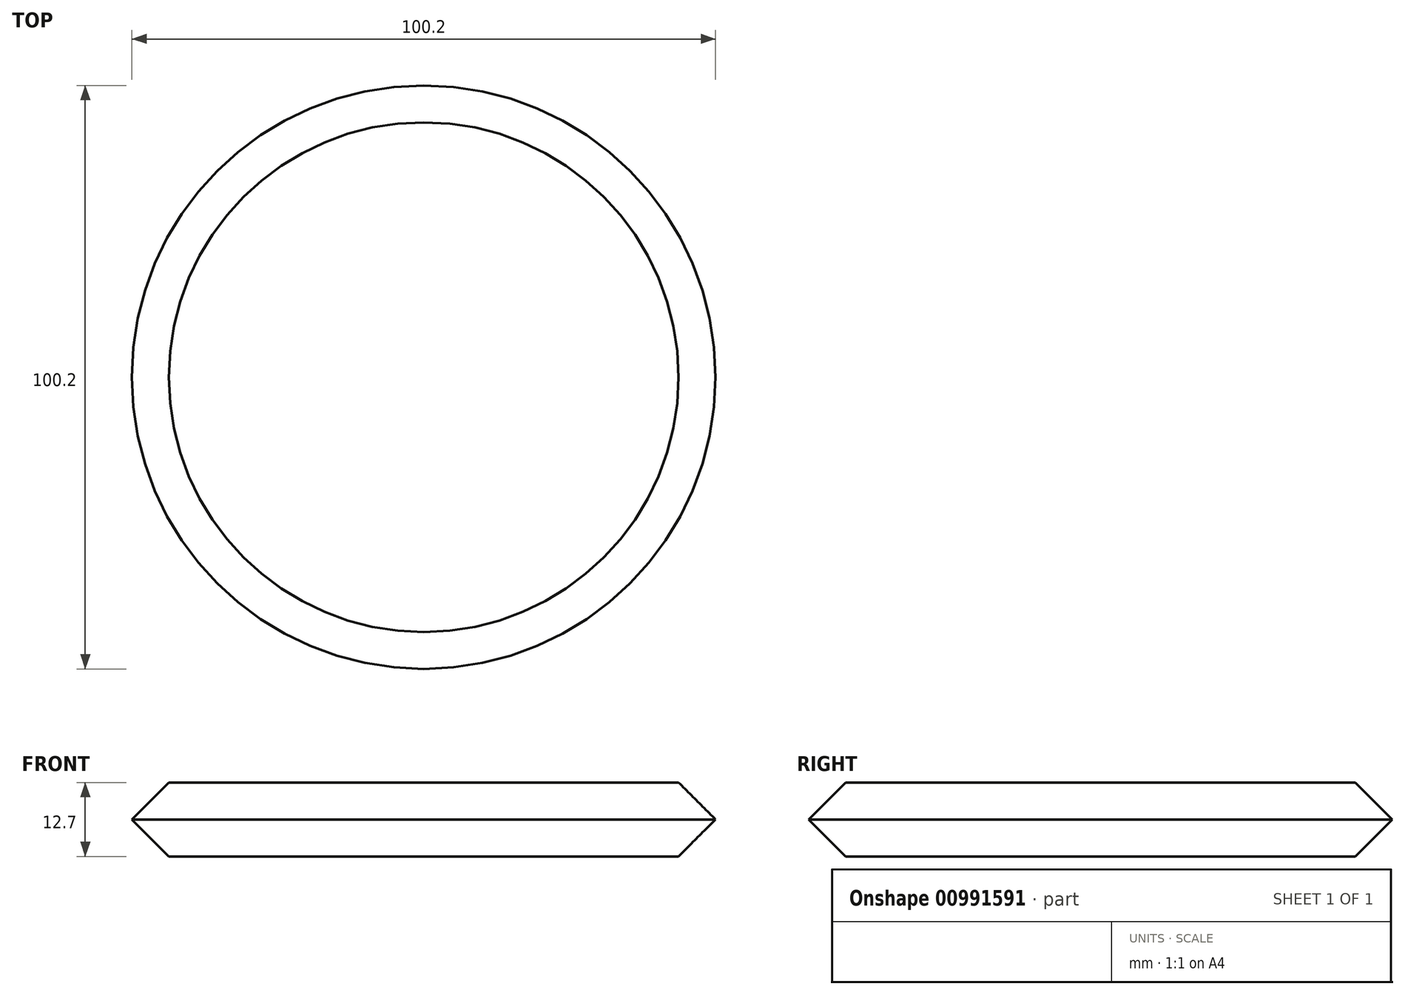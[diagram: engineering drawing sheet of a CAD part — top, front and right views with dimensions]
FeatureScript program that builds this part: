
annotation { "Feature Type Name" : "Feature", "Feature Type Description" : "" }
export const myFeature = defineFeature(function(context is Context, id is Id, definition is map)
    precondition{}
    {
        {
            var Q0;
            Q0=qCreatedBy(makeId("Top.planeOp"),FACE);
            var sketch = newSketch(context, id + "F0", { "sketchPlane" : qUnion([Q0])});
            skCircle(sketch, "E0", {"center": v(-3.31, -2.78) * mm, "radius": 50.1 * mm});
            skPoint(sketch, "E0.first.point", {"position": v(35.32, -34.68) * mm});
            skPoint(sketch, "E0.second.point", {"position": v(-41.78, 29.32) * mm});
            skPoint(sketch, "E0.third.point", {"position": v(22.09, 40.4) * mm});
            skSolve(sketch);
        }
        {
            var Q0;
            Q0=makeQuery(id+"F0.imprint","IMPRINT",FACE,{"disambiguationData":[TD([[makeQuery(id+"F0.imprint","IMPRINT",EDGE,{"derivedFrom":sQuery(id+"F0.wireOp",EDGE,"E0")}),1.0]])]});
            extrude(context, id + "F1", {"entities" : qUnion([Q0]), "depth" : 12.7 * mm, "offsetDistance" : 25.4 * mm});
        }
        {
            var Q0;
            Q0=makeQuery(id+"F1.opExtrude","CAP_FACE",FACE,{"disambiguationData":[OSD([sQuery(id+"F0.wireOp",EDGE,"E0")])],"isStart":false});
            chamfer(context, id + "F2", {"entities" : qUnion([Q0]), "width" : 6.35 * mm, "tangentPropagation" : true});
        }
        {
            var Q0;
            Q0=makeQuery(id+"F1.opExtrude","CAP_EDGE",EDGE,{"disambiguationData":[OSD([sQuery(id+"F0.wireOp",EDGE,"E0")])],"isStart":true});
            chamfer(context, id + "F3", {"entities" : qUnion([Q0]), "width" : 6.35 * mm, "tangentPropagation" : true});
        }
    });
